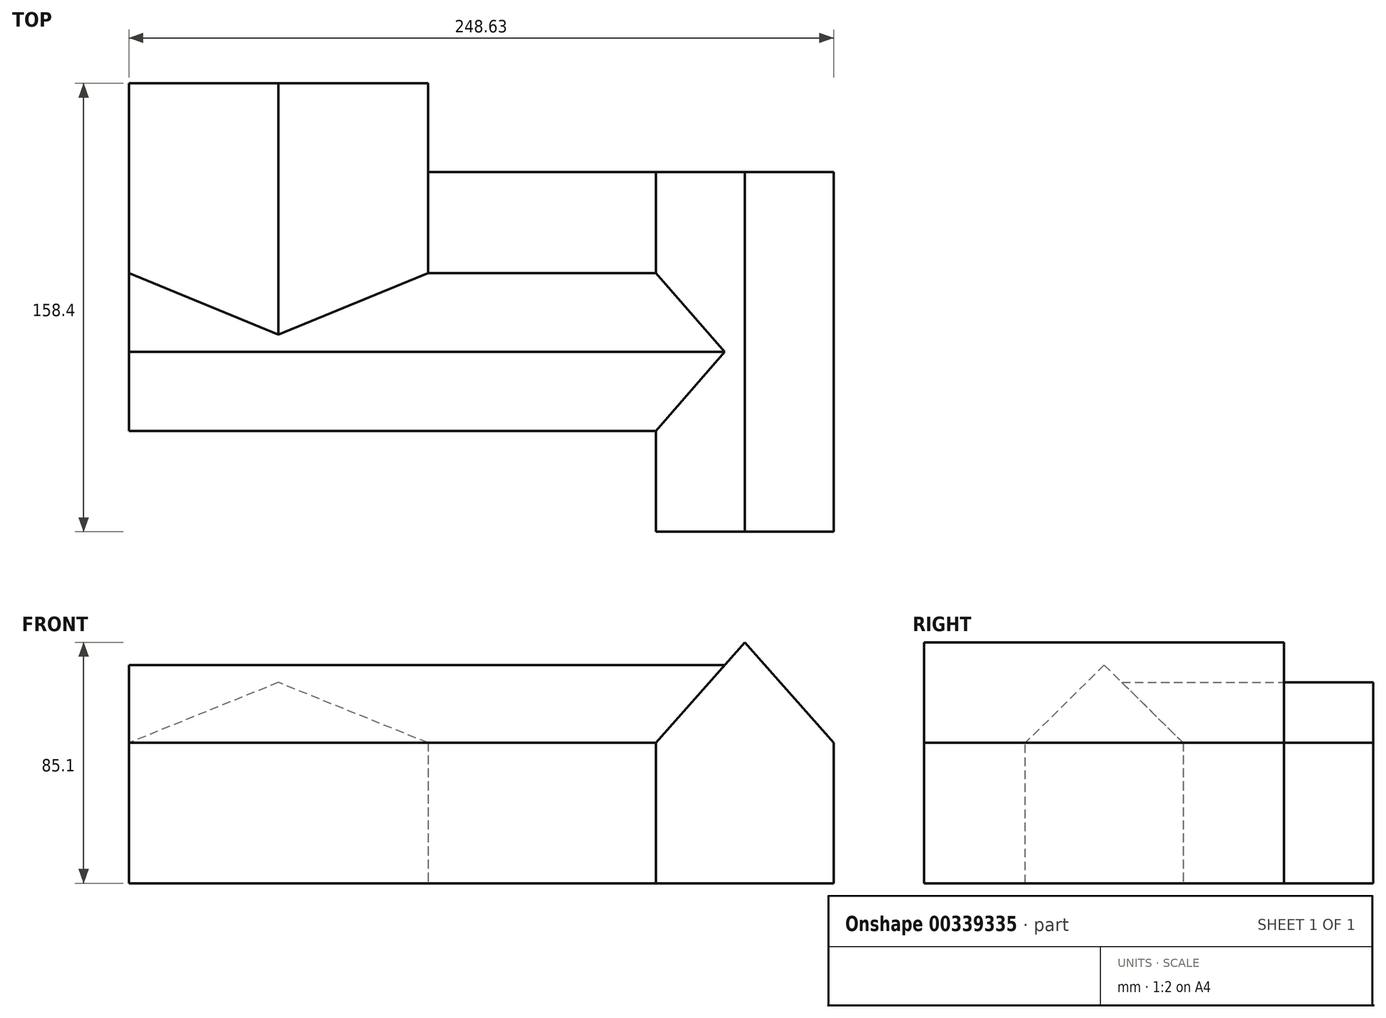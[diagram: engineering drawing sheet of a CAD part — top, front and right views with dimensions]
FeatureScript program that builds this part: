
annotation { "Feature Type Name" : "Feature", "Feature Type Description" : "" }
export const myFeature = defineFeature(function(context is Context, id is Id, definition is map)
    precondition{}
    {
        {
            var Q0;
            Q0=qCreatedBy(makeId("Front.planeOp"),FACE);
            var sketch = newSketch(context, id + "F0", { "sketchPlane" : qUnion([Q0])});
            skLineSegment(sketch, "E0", {"start": v(0, 0) * mm, "end": v(0, 49.58) * mm});
            skLineSegment(sketch, "E1", {"start": v(0, 49.58) * mm, "end": v(31.35, 85.1) * mm});
            skLineSegment(sketch, "E2", {"start": v(31.35, 85.1) * mm, "end": v(62.7, 49.58) * mm});
            skLineSegment(sketch, "E3", {"start": v(62.7, 49.58) * mm, "end": v(62.7, 0) * mm});
            skLineSegment(sketch, "E4", {"start": v(62.7, 0) * mm, "end": v(0, 0) * mm});
            skLineSegment(sketch, "E5", {"start": v(0, 49.58) * mm, "end": v(62.7, 49.58) * mm});
            skLineSegment(sketch, "E6", {"start": v(31.35, 49.58) * mm, "end": v(31.35, 85.1) * mm, "construction": true});
            skSolve(sketch);
        }
        {
            var Q0;
            Q0 = qSketchRegion(id + "F0", true);
            extrude(context, id + "F1", {"entities" : qUnion([Q0]), "depth" : 127 * mm});
        }
        {
            var Q0;
            Q0=makeQuery(id+"F1.opExtrude","SWEPT_FACE",FACE,{"disambiguationData":[OSD([sQuery(id+"F0.wireOp",EDGE,"E0")])]});
            var sketch = newSketch(context, id + "F2", { "sketchPlane" : qUnion([Q0])});
            skLineSegment(sketch, "E7", {"start": v(63.5, 0) * mm, "end": v(63.5, 77.05) * mm, "construction": true});
            skPoint(sketch, "E7.endSnap0", {"position": v(63.5, 49.58) * mm});
            skLineSegment(sketch, "E8", {"start": v(63.5, 77.05) * mm, "end": v(35.66, 49.58) * mm});
            skLineSegment(sketch, "E9", {"start": v(35.66, 49.58) * mm, "end": v(35.66, 0) * mm});
            skLineSegment(sketch, "E10", {"start": v(35.66, 0) * mm, "end": v(91.34, 0) * mm});
            skLineSegment(sketch, "E11", {"start": v(91.34, 0) * mm, "end": v(91.34, 49.58) * mm});
            skLineSegment(sketch, "E12", {"start": v(91.34, 49.58) * mm, "end": v(63.5, 77.05) * mm});
            skSolve(sketch);
        }
        {
            var Q0;
            Q0 = qSketchRegion(id + "F2", true);
            var Q1;
            Q1=makeQuery(id+"F1.opExtrude","SWEPT_FACE",FACE,{"disambiguationData":[OSD([sQuery(id+"F0.wireOp",EDGE,"E1")])]});
            extrude(context, id + "F3", {"entities" : qUnion([Q0]), "operationType" : NewBodyOperationType.ADD, "endBound" : BoundingType.UP_TO_SURFACE, "oppositeDirection" : true, "endBoundEntityFace" : qUnion([Q1]), "depth" : 25.4 * mm});
        }
        {
            var Q0;
            Q0 = qSketchRegion(id + "F2", true);
            extrude(context, id + "F4", {"entities" : qUnion([Q0]), "operationType" : NewBodyOperationType.ADD, "depth" : 185.93 * mm});
        }
        {
            var Q0;
            Q0=makeQuery(id+"F4.opExtrude","SWEPT_FACE",FACE,{"disambiguationData":[OSD([sQuery(id+"F2.wireOp",EDGE,"E9")])]});
            var sketch = newSketch(context, id + "F5", { "sketchPlane" : qUnion([Q0])});
            skLineSegment(sketch, "E13", {"start": v(185.93, 0) * mm, "end": v(185.93, 49.58) * mm});
            skLineSegment(sketch, "E14", {"start": v(185.93, 49.58) * mm, "end": v(133.16, 70.93) * mm});
            skLineSegment(sketch, "E15", {"start": v(133.16, 70.93) * mm, "end": v(80.4, 49.58) * mm});
            skLineSegment(sketch, "E16", {"start": v(80.4, 49.58) * mm, "end": v(80.4, 0) * mm});
            skLineSegment(sketch, "E17", {"start": v(80.4, 0) * mm, "end": v(185.93, 0) * mm});
            skSolve(sketch);
        }
        {
            var Q0;
            {var subQ0=sQuery(id+"F5.wireOp",EDGE,"E14");Q0=makeQuery(id+"F5.imprint","IMPRINT",FACE,{"disambiguationData":[TD([[makeQuery(id+"F5.imprint","IMPRINT",EDGE,{"derivedFrom":subQ0}),1.0]])]});}
            var Q1;
            {var subQ0=sQuery(id+"F2.wireOp",EDGE,"E8");Q1=makeQuery(id+"F4.boolean.opBoolean","MERGE",FACE,{"derivedFrom":[makeQuery(id+"F3.opExtrude","SWEPT_FACE",FACE,{"disambiguationData":[OSD([subQ0])]}),makeQuery(id+"F4.opExtrude","SWEPT_FACE",FACE,{"disambiguationData":[OSD([subQ0])]})]});}
            extrude(context, id + "F6", {"entities" : qUnion([Q0]), "operationType" : NewBodyOperationType.ADD, "endBound" : BoundingType.UP_TO_SURFACE, "oppositeDirection" : true, "endBoundEntityFace" : qUnion([Q1]), "depth" : 25.4 * mm});
        }
        {
            var Q0;
            Q0 = qSketchRegion(id + "F5", true);
            extrude(context, id + "F7", {"entities" : qUnion([Q0]), "operationType" : NewBodyOperationType.ADD, "depth" : 67.06 * mm});
        }
        {
            var Q0;
            Q0=makeQuery(id+"F7.boolean.opBoolean","MERGE",FACE,{"derivedFrom":[makeQuery(id+"F4.boolean.opBoolean","MERGE",FACE,{"derivedFrom":[makeQuery(id+"F1.opExtrude","SWEPT_FACE",FACE,{"disambiguationData":[OSD([sQuery(id+"F0.wireOp",EDGE,"E4")])]}),makeQuery(id+"F4.opExtrude","SWEPT_FACE",FACE,{"disambiguationData":[OSD([sQuery(id+"F2.wireOp",EDGE,"E10")])]})]}),makeQuery(id+"F7.opExtrude","SWEPT_FACE",FACE,{"disambiguationData":[OSD([sQuery(id+"F5.wireOp",EDGE,"E17")])]})]});
            var sketch = newSketch(context, id + "F8", { "sketchPlane" : qUnion([Q0])});
            skLineSegment(sketch, "E18.bottom", {"start": v(0, 0) * mm, "end": v(-80.4, 0) * mm});
            skLineSegment(sketch, "E18.top", {"start": v(0, 35.66) * mm, "end": v(-80.4, 35.66) * mm});
            skLineSegment(sketch, "E18.left", {"start": v(0, 0) * mm, "end": v(0, 35.66) * mm});
            skLineSegment(sketch, "E18.right", {"start": v(-80.4, 0) * mm, "end": v(-80.4, 35.66) * mm});
            skSolve(sketch);
        }
        {
            var Q0;
            Q0=makeQuery(id+"F8.imprint","IMPRINT",FACE,{"disambiguationData":[TD([[makeQuery(id+"F8.imprint","IMPRINT",EDGE,{"derivedFrom":sQuery(id+"F8.wireOp",EDGE,"E18.bottom")}),-1.0]])]});
            var Q1;
            {var subQ0=sQuery(id+"F2.wireOp",EDGE,"E8");Q1=makeQuery(id+"F4.boolean.opBoolean","MERGE",FACE,{"derivedFrom":[makeQuery(id+"F3.opExtrude","SWEPT_FACE",FACE,{"disambiguationData":[OSD([subQ0])]}),makeQuery(id+"F4.opExtrude","SWEPT_FACE",FACE,{"disambiguationData":[OSD([subQ0])]})]});}
            extrude(context, id + "F9", {"entities" : qUnion([Q0]), "oppositeDirection" : true, "endBoundEntityFace" : qUnion([Q1]), "depth" : 49.78 * mm});
        }
    });
